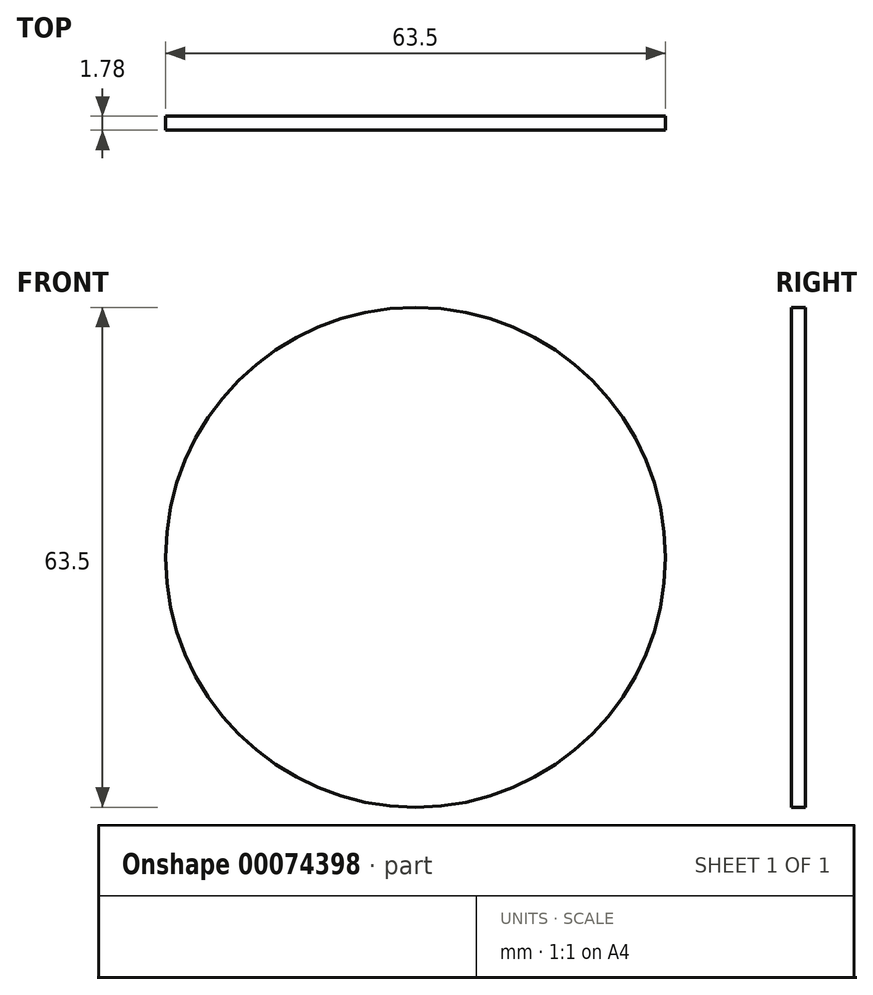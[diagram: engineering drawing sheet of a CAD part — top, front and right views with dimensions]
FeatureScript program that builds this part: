
annotation { "Feature Type Name" : "Feature", "Feature Type Description" : "" }
export const myFeature = defineFeature(function(context is Context, id is Id, definition is map)
    precondition{}
    {
        {
            var Q0;
            Q0=qCreatedBy(makeId("Front.planeOp"),FACE);
            var sketch = newSketch(context, id + "F0", { "sketchPlane" : qUnion([Q0])});
            skCircle(sketch, "E0", {"center": v(0, 0) * mm, "radius": 31.75 * mm});
            skSolve(sketch);
        }
        {
            var Q0;
            Q0=makeQuery(id+"F0.imprint","IMPRINT",FACE,{"disambiguationData":[TD([[makeQuery(id+"F0.imprint","IMPRINT",EDGE,{"derivedFrom":sQuery(id+"F0.wireOp",EDGE,"E0")}),1.0]])]});
            extrude(context, id + "F1", {"entities" : qUnion([Q0]), "depth" : 1.78 * mm});
        }
    });
